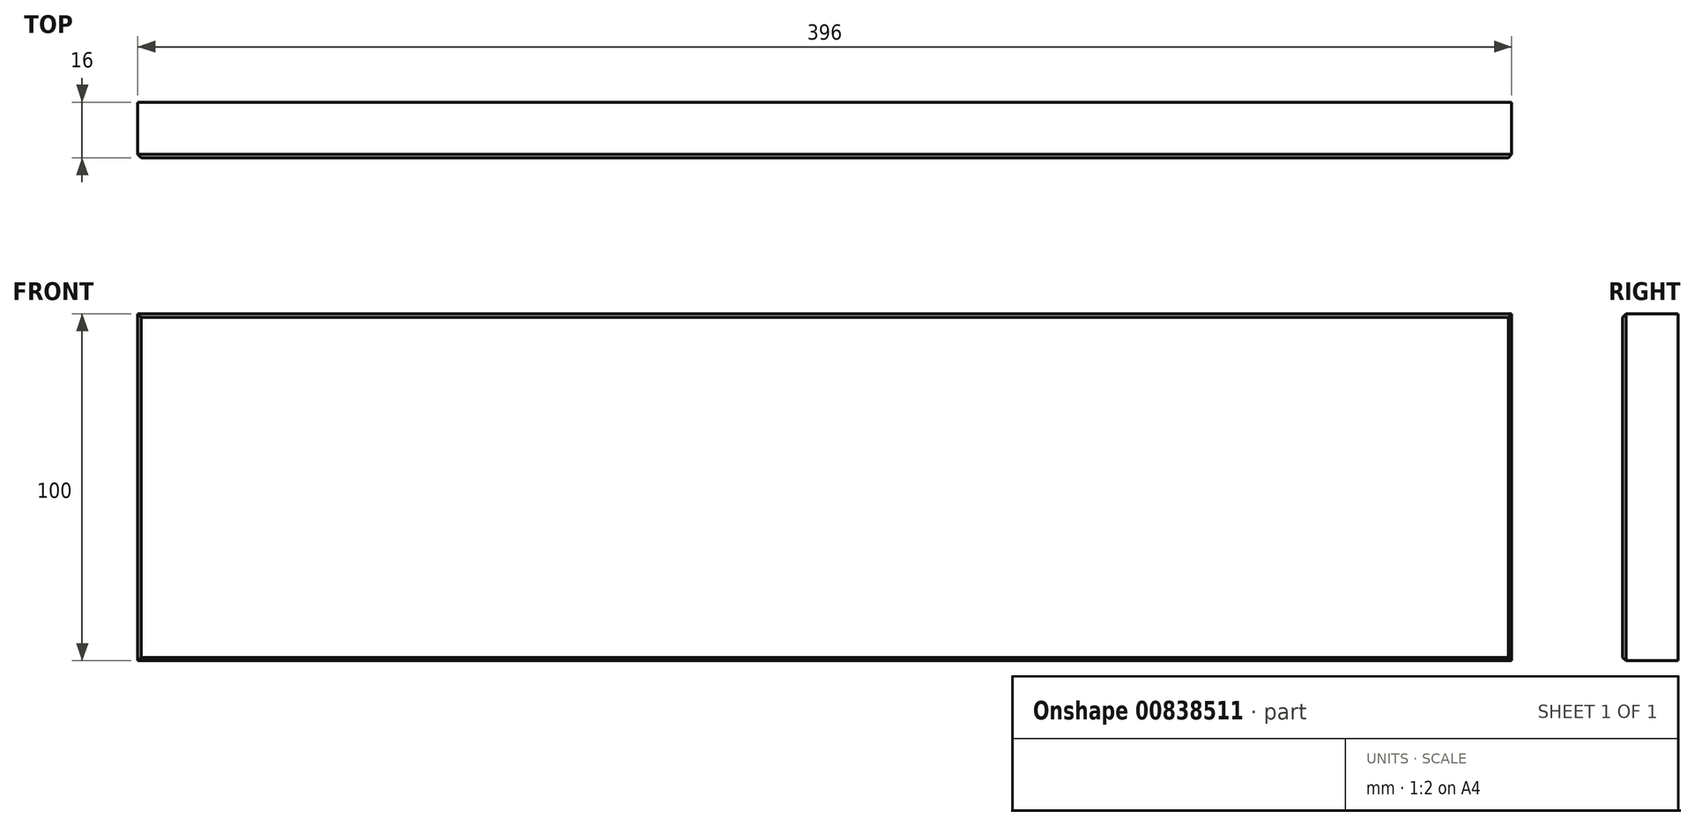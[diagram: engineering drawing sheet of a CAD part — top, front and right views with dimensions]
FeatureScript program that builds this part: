
annotation { "Feature Type Name" : "Feature", "Feature Type Description" : "" }
export const myFeature = defineFeature(function(context is Context, id is Id, definition is map)
    precondition{}
    {
        {
            var Q0;
            Q0=qCreatedBy(makeId("Front.planeOp"),FACE);
            var sketch = newSketch(context, id + "F0", { "sketchPlane" : qUnion([Q0])});
            skLineSegment(sketch, "E0.bottom", {"start": v(0, 0) * mm, "end": v(43.57, 0) * mm});
            skLineSegment(sketch, "E0.top", {"start": v(0, 38.66) * mm, "end": v(43.57, 38.66) * mm});
            skLineSegment(sketch, "E0.left", {"start": v(0, 0) * mm, "end": v(0, 38.66) * mm});
            skLineSegment(sketch, "E0.right", {"start": v(43.57, 0) * mm, "end": v(43.57, 38.66) * mm});
            skSolve(sketch);
        }
        {
            var Q0;
            Q0=makeQuery(id+"F0.imprint","IMPRINT",FACE,{"disambiguationData":[TD([[makeQuery(id+"F0.imprint","IMPRINT",EDGE,{"derivedFrom":sQuery(id+"F0.wireOp",EDGE,"E0.bottom")}),1.0]])]});
            extrude(context, id + "F1", {"entities" : qUnion([Q0]), "depth" : 16 * mm, "offsetDistance" : 25.4 * mm});
        }
        {
            var Q0;
            Q0=makeQuery(id+"F1.opExtrude","SWEPT_FACE",FACE,{"disambiguationData":[OSD([sQuery(id+"F0.wireOp",EDGE,"E0.left")])]});
            extrude(context, id + "F2", {"entities" : qUnion([Q0]), "operationType" : NewBodyOperationType.ADD, "oppositeDirection" : true, "depth" : 396 * mm, "offsetDistance" : 25 * mm});
        }
        {
            var Q0;
            {var subQ0=sQuery(id+"F0.wireOp",EDGE,"E0.bottom");Q0=makeQuery(id+"F2.boolean.opBoolean","MERGE",FACE,{"derivedFrom":[makeQuery(id+"F1.opExtrude","SWEPT_FACE",FACE,{"disambiguationData":[OSD([subQ0])]}),makeQuery(id+"F2.opExtrude","SWEPT_FACE",FACE,{"disambiguationData":[OSD([subQ0,sQuery(id+"F0.wireOp",EDGE,"E0.left")])]})]});}
            extrude(context, id + "F3", {"entities" : qUnion([Q0]), "operationType" : NewBodyOperationType.ADD, "oppositeDirection" : true, "depth" : 100 * mm, "offsetDistance" : 25 * mm});
        }
        {
            var Q0;
            {var subQ0=sQuery(id+"F0.wireOp",EDGE,"E0.left");var subQ1=sQuery(id+"F0.wireOp",EDGE,"E0.bottom");Q0=makeQuery(id+"F3.boolean.opBoolean","MERGE",FACE,{"derivedFrom":[makeQuery(id+"F2.boolean.opBoolean","MERGE",FACE,{"derivedFrom":[makeQuery(id+"F1.opExtrude","CAP_FACE",FACE,{"disambiguationData":[OSD([subQ1,sQuery(id+"F0.wireOp",EDGE,"E0.top"),subQ0,sQuery(id+"F0.wireOp",EDGE,"E0.right")])],"isStart":false}),makeQuery(id+"F2.opExtrude","SWEPT_FACE",FACE,{"disambiguationData":[OSD([subQ0]),TDD([makeQuery(id+"F1.opExtrude","CAP_EDGE",EDGE,{"disambiguationData":[OSD([subQ0])],"isStart":false})])]})]}),makeQuery(id+"F3.opExtrude","SWEPT_FACE",FACE,{"disambiguationData":[OSD([subQ1,subQ0]),TDD([makeQuery(id+"F2.boolean.opBoolean","MERGE",EDGE,{"derivedFrom":[makeQuery(id+"F1.opExtrude","CAP_EDGE",EDGE,{"disambiguationData":[OSD([subQ1])],"isStart":false}),makeQuery(id+"F2.opExtrude","SWEPT_EDGE",EDGE,{"disambiguationData":[OSD([subQ1,subQ0]),TDD([makeQuery(id+"F1.opExtrude","CAP_VERTEX",VERTEX,{"disambiguationData":[OSD([subQ1,subQ0])],"isStart":false})])]})]})])]})]});}
            chamfer(context, id + "F4", {"entities" : qUnion([Q0]), "width" : 1 * mm, "tangentPropagation" : true});
        }
    });
